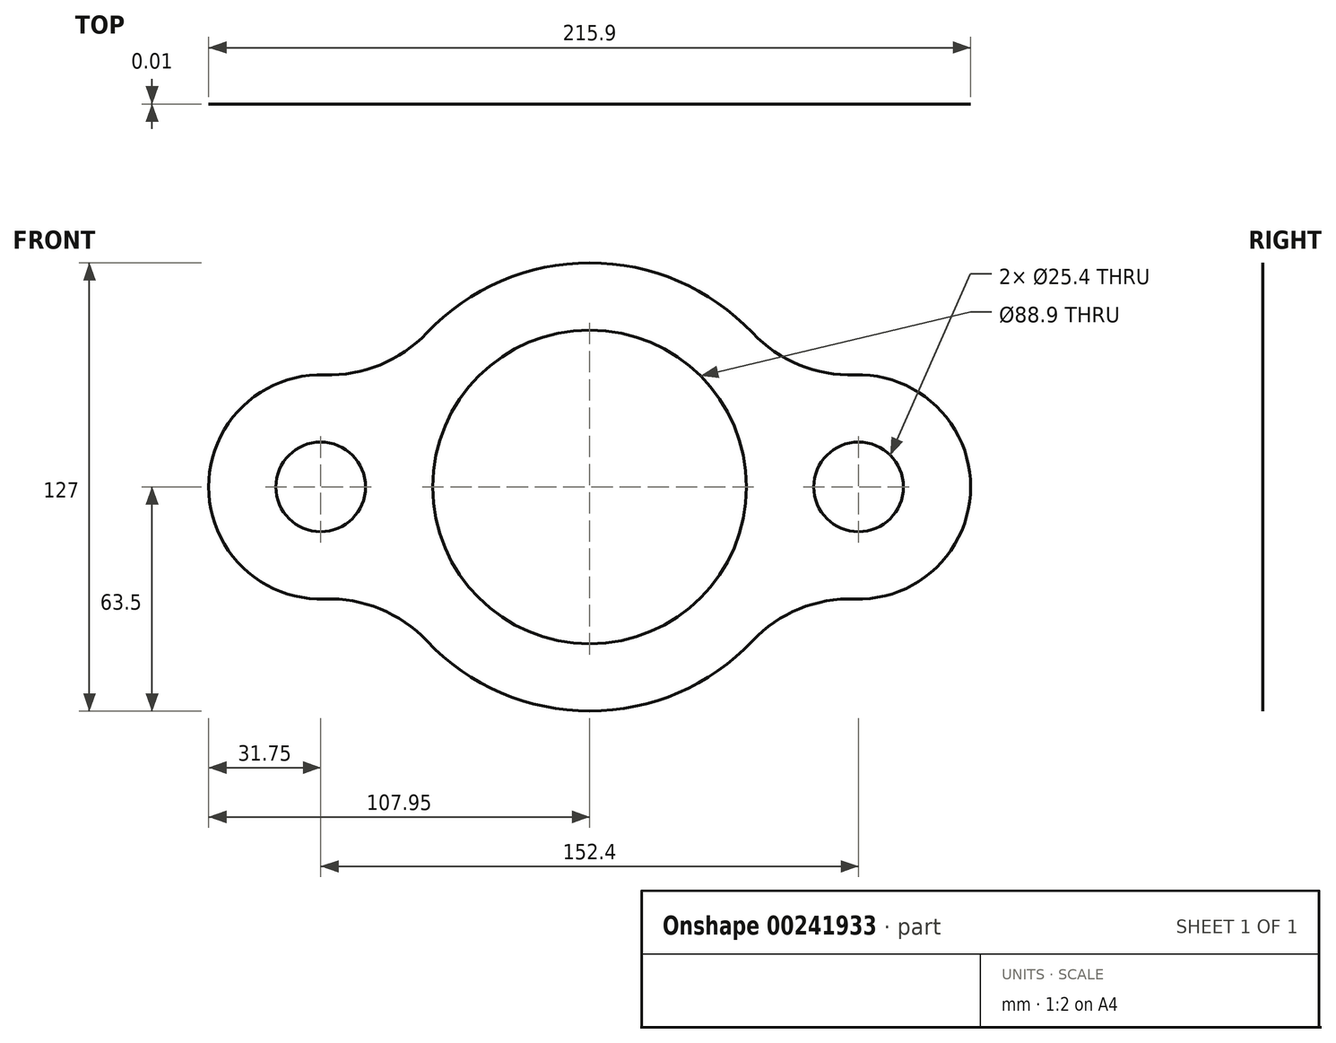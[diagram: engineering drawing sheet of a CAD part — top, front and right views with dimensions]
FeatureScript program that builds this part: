
annotation { "Feature Type Name" : "Feature", "Feature Type Description" : "" }
export const myFeature = defineFeature(function(context is Context, id is Id, definition is map)
    precondition{}
    {
        {
            var Q0;
            Q0=qCreatedBy(makeId("Front.planeOp"),FACE);
            var sketch = newSketch(context, id + "F0", { "sketchPlane" : qUnion([Q0])});
            skArc(sketch, "E0", {"start": v(-46.14, -43.63) * mm, "mid": v(0, -63.5) * mm, "end": v(46.14, -43.63) * mm});
            skCircle(sketch, "E1", {"center": v(0, 0) * mm, "radius": 44.45 * mm});
            skCircle(sketch, "E2", {"center": v(76.2, 0) * mm, "radius": 12.7 * mm});
            skArc(sketch, "E3", {"start": v(75.12, -31.73) * mm, "mid": v(107.95, 0) * mm, "end": v(75.12, 31.73) * mm});
            skCircle(sketch, "E4", {"center": v(-76.2, 0) * mm, "radius": 12.7 * mm});
            skArc(sketch, "E5", {"start": v(-75.12, 31.73) * mm, "mid": v(-107.95, 0) * mm, "end": v(-75.12, -31.73) * mm});
            skArc(sketch, "E6.trimOffspring", {"start": v(46.14, 43.63) * mm, "mid": v(0, 63.5) * mm, "end": v(-46.14, 43.63) * mm});
            skPoint(sketch, "E7.visualSharp", {"position": v(-57.94, 25.98) * mm});
            skArc(sketch, "E7.filletArc", {"start": v(-75.12, 31.73) * mm, "mid": v(-59.35, 34.56) * mm, "end": v(-46.14, 43.63) * mm});
            skPoint(sketch, "E8.visualSharp", {"position": v(57.94, 25.98) * mm});
            skArc(sketch, "E8.filletArc", {"start": v(46.14, 43.63) * mm, "mid": v(59.35, 34.56) * mm, "end": v(75.12, 31.73) * mm});
            skPoint(sketch, "E9.visualSharp", {"position": v(57.94, -25.98) * mm});
            skArc(sketch, "E9.filletArc", {"start": v(75.12, -31.73) * mm, "mid": v(59.35, -34.56) * mm, "end": v(46.14, -43.63) * mm});
            skPoint(sketch, "E10.visualSharp", {"position": v(-57.94, -25.98) * mm});
            skArc(sketch, "E10.filletArc", {"start": v(-46.14, -43.63) * mm, "mid": v(-59.35, -34.56) * mm, "end": v(-75.12, -31.73) * mm});
            skSolve(sketch);
        }
        {
            var Q0;
            Q0 = qSketchRegion(id + "F0", true);
            extrude(context, id + "F1", {"entities" : qUnion([Q0]), "depth" : 1 / 101.6 * mm});
        }
    });
